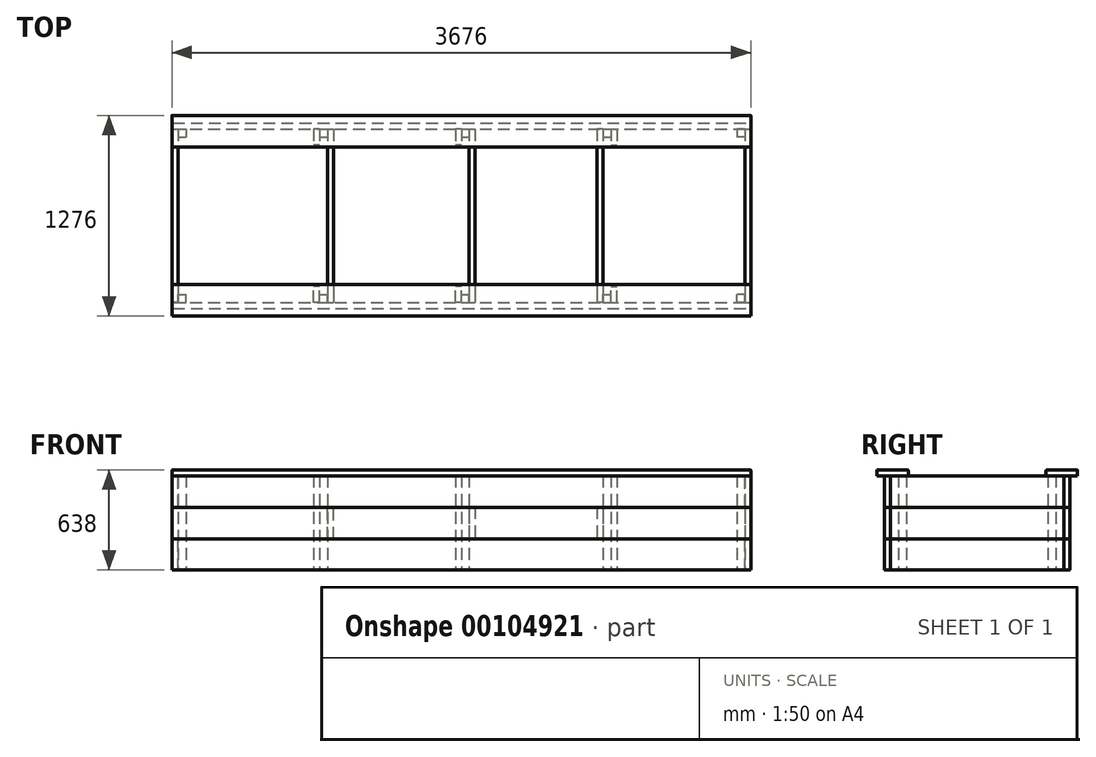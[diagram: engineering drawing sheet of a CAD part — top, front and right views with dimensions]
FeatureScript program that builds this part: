
annotation { "Feature Type Name" : "Feature", "Feature Type Description" : "" }
export const myFeature = defineFeature(function(context is Context, id is Id, definition is map)
    precondition{}
    {
        {
            var Q0;
            Q0=qCreatedBy(makeId("Top.planeOp"),FACE);
            var sketch = newSketch(context, id + "F0", { "sketchPlane" : qUnion([Q0])});
            skLineSegment(sketch, "E0", {"start": v(-110.58, 50) * mm, "end": v(3489.42, 50) * mm, "construction": true});
            skLineSegment(sketch, "E1", {"start": v(3489.42, 50) * mm, "end": v(3489.42, -1050) * mm, "construction": true});
            skLineSegment(sketch, "E2", {"start": v(3489.42, -1050) * mm, "end": v(-110.58, -1050) * mm, "construction": true});
            skLineSegment(sketch, "E3", {"start": v(-110.58, -1050) * mm, "end": v(-110.58, 50) * mm, "construction": true});
            skLineSegment(sketch, "E4.bottom", {"start": v(-110.58, 50) * mm, "end": v(-60.58, 50) * mm});
            skLineSegment(sketch, "E4.top", {"start": v(-110.58, 0) * mm, "end": v(-60.58, 0) * mm});
            skLineSegment(sketch, "E4.left", {"start": v(-110.58, 50) * mm, "end": v(-110.58, 0) * mm});
            skLineSegment(sketch, "E4.right", {"start": v(-60.58, 50) * mm, "end": v(-60.58, 0) * mm});
            skLineSegment(sketch, "E5.bottom", {"start": v(-110.58, -1050) * mm, "end": v(-60.58, -1050) * mm});
            skLineSegment(sketch, "E5.top", {"start": v(-110.58, -1000) * mm, "end": v(-60.58, -1000) * mm});
            skLineSegment(sketch, "E5.left", {"start": v(-110.58, -1050) * mm, "end": v(-110.58, -1000) * mm});
            skLineSegment(sketch, "E5.right", {"start": v(-60.58, -1050) * mm, "end": v(-60.58, -1000) * mm});
            skLineSegment(sketch, "E6.bottom", {"start": v(3489.42, -1050) * mm, "end": v(3439.42, -1050) * mm});
            skLineSegment(sketch, "E6.top", {"start": v(3489.42, -1000) * mm, "end": v(3439.42, -1000) * mm});
            skLineSegment(sketch, "E6.left", {"start": v(3489.42, -1050) * mm, "end": v(3489.42, -1000) * mm});
            skLineSegment(sketch, "E6.right", {"start": v(3439.42, -1050) * mm, "end": v(3439.42, -1000) * mm});
            skLineSegment(sketch, "E7.bottom", {"start": v(3489.42, 50) * mm, "end": v(3439.42, 50) * mm});
            skLineSegment(sketch, "E7.top", {"start": v(3489.42, 0) * mm, "end": v(3439.42, 0) * mm});
            skLineSegment(sketch, "E7.left", {"start": v(3489.42, 50) * mm, "end": v(3489.42, 0) * mm});
            skLineSegment(sketch, "E7.right", {"start": v(3439.42, 50) * mm, "end": v(3439.42, 0) * mm});
            skLineSegment(sketch, "E8.bottom", {"start": v(789.42, -1050) * mm, "end": v(839.42, -1050) * mm});
            skLineSegment(sketch, "E8.top", {"start": v(789.42, -1000) * mm, "end": v(839.42, -1000) * mm});
            skLineSegment(sketch, "E8.left", {"start": v(789.42, -1050) * mm, "end": v(789.42, -1000) * mm});
            skLineSegment(sketch, "E8.right", {"start": v(839.42, -1050) * mm, "end": v(839.42, -1000) * mm});
            skLineSegment(sketch, "E9.bottom", {"start": v(1689.42, -1050) * mm, "end": v(1739.42, -1050) * mm});
            skLineSegment(sketch, "E9.top", {"start": v(1689.42, -1000) * mm, "end": v(1739.42, -1000) * mm});
            skLineSegment(sketch, "E9.left", {"start": v(1689.42, -1050) * mm, "end": v(1689.42, -1000) * mm});
            skLineSegment(sketch, "E9.right", {"start": v(1739.42, -1050) * mm, "end": v(1739.42, -1000) * mm});
            skLineSegment(sketch, "E10.bottom", {"start": v(2589.42, -1050) * mm, "end": v(2639.42, -1050) * mm});
            skLineSegment(sketch, "E10.top", {"start": v(2589.42, -1000) * mm, "end": v(2639.42, -1000) * mm});
            skLineSegment(sketch, "E10.left", {"start": v(2589.42, -1050) * mm, "end": v(2589.42, -1000) * mm});
            skLineSegment(sketch, "E10.right", {"start": v(2639.42, -1050) * mm, "end": v(2639.42, -1000) * mm});
            skLineSegment(sketch, "E11.bottom", {"start": v(789.42, 50) * mm, "end": v(839.42, 50) * mm});
            skLineSegment(sketch, "E11.top", {"start": v(789.42, 0) * mm, "end": v(839.42, 0) * mm});
            skLineSegment(sketch, "E11.left", {"start": v(789.42, 50) * mm, "end": v(789.42, 0) * mm});
            skLineSegment(sketch, "E11.right", {"start": v(839.42, 50) * mm, "end": v(839.42, 0) * mm});
            skLineSegment(sketch, "E12.bottom", {"start": v(1689.42, 50) * mm, "end": v(1739.42, 50) * mm});
            skLineSegment(sketch, "E12.top", {"start": v(1689.42, 0) * mm, "end": v(1739.42, 0) * mm});
            skLineSegment(sketch, "E12.left", {"start": v(1689.42, 50) * mm, "end": v(1689.42, 0) * mm});
            skLineSegment(sketch, "E12.right", {"start": v(1739.42, 50) * mm, "end": v(1739.42, 0) * mm});
            skLineSegment(sketch, "E13.bottom", {"start": v(2589.42, 50) * mm, "end": v(2639.42, 50) * mm});
            skLineSegment(sketch, "E13.top", {"start": v(2589.42, 0) * mm, "end": v(2639.42, 0) * mm});
            skLineSegment(sketch, "E13.left", {"start": v(2589.42, 50) * mm, "end": v(2589.42, 0) * mm});
            skLineSegment(sketch, "E13.right", {"start": v(2639.42, 50) * mm, "end": v(2639.42, 0) * mm});
            skLineSegment(sketch, "E14.bottom", {"start": v(789.42, 50) * mm, "end": v(751.42, 50) * mm});
            skLineSegment(sketch, "E14.top", {"start": v(789.42, -50) * mm, "end": v(751.42, -50) * mm});
            skLineSegment(sketch, "E14.left", {"start": v(789.42, 50) * mm, "end": v(789.42, -50) * mm});
            skLineSegment(sketch, "E14.right", {"start": v(751.42, 50) * mm, "end": v(751.42, -50) * mm});
            skLineSegment(sketch, "E15.bottom", {"start": v(1689.42, 50) * mm, "end": v(1651.42, 50) * mm});
            skLineSegment(sketch, "E15.top", {"start": v(1689.42, -50) * mm, "end": v(1651.42, -50) * mm});
            skLineSegment(sketch, "E15.left", {"start": v(1689.42, 50) * mm, "end": v(1689.42, -50) * mm});
            skLineSegment(sketch, "E15.right", {"start": v(1651.42, 50) * mm, "end": v(1651.42, -50) * mm});
            skLineSegment(sketch, "E16.bottom", {"start": v(789.42, -1050) * mm, "end": v(751.42, -1050) * mm});
            skLineSegment(sketch, "E16.top", {"start": v(789.42, -950) * mm, "end": v(751.42, -950) * mm});
            skLineSegment(sketch, "E16.left", {"start": v(789.42, -1050) * mm, "end": v(789.42, -950) * mm});
            skLineSegment(sketch, "E16.right", {"start": v(751.42, -1050) * mm, "end": v(751.42, -950) * mm});
            skLineSegment(sketch, "E17.bottom", {"start": v(1689.42, -1050) * mm, "end": v(1651.42, -1050) * mm});
            skLineSegment(sketch, "E17.top", {"start": v(1689.42, -950) * mm, "end": v(1651.42, -950) * mm});
            skLineSegment(sketch, "E17.left", {"start": v(1689.42, -1050) * mm, "end": v(1689.42, -950) * mm});
            skLineSegment(sketch, "E17.right", {"start": v(1651.42, -1050) * mm, "end": v(1651.42, -950) * mm});
            skLineSegment(sketch, "E18.bottom", {"start": v(2639.42, 50) * mm, "end": v(2677.42, 50) * mm});
            skLineSegment(sketch, "E18.top", {"start": v(2639.42, -50) * mm, "end": v(2677.42, -50) * mm});
            skLineSegment(sketch, "E18.left", {"start": v(2639.42, 50) * mm, "end": v(2639.42, -50) * mm});
            skLineSegment(sketch, "E18.right", {"start": v(2677.42, 50) * mm, "end": v(2677.42, -50) * mm});
            skLineSegment(sketch, "E19.bottom", {"start": v(2639.42, -1050) * mm, "end": v(2677.42, -1050) * mm});
            skLineSegment(sketch, "E19.top", {"start": v(2639.42, -950) * mm, "end": v(2677.42, -950) * mm});
            skLineSegment(sketch, "E19.left", {"start": v(2639.42, -1050) * mm, "end": v(2639.42, -950) * mm});
            skLineSegment(sketch, "E19.right", {"start": v(2677.42, -1050) * mm, "end": v(2677.42, -950) * mm});
            skSolve(sketch);
        }
        {
            var Q0;
            Q0=makeQuery(id+"F0.imprint","IMPRINT",FACE,{"disambiguationData":[TD([[makeQuery(id+"F0.imprint","IMPRINT",EDGE,{"derivedFrom":sQuery(id+"F0.wireOp",EDGE,"E4.bottom")}),-1.0]])]});
            var Q1;
            {var subQ0=sQuery(id+"F0.wireOp",EDGE,"E11.bottom");Q1=makeQuery(id+"F0.imprint","IMPRINT",FACE,{"disambiguationData":[TD([[makeQuery(id+"F0.imprint","IMPRINT",EDGE,{"derivedFrom":subQ0}),-1.0]])]});}
            var Q2;
            {var subQ0=sQuery(id+"F0.wireOp",EDGE,"E12.bottom");Q2=makeQuery(id+"F0.imprint","IMPRINT",FACE,{"disambiguationData":[TD([[makeQuery(id+"F0.imprint","IMPRINT",EDGE,{"derivedFrom":subQ0}),-1.0]])]});}
            var Q3;
            {var subQ0=sQuery(id+"F0.wireOp",EDGE,"E13.bottom");Q3=makeQuery(id+"F0.imprint","IMPRINT",FACE,{"disambiguationData":[TD([[makeQuery(id+"F0.imprint","IMPRINT",EDGE,{"derivedFrom":subQ0}),-1.0]])]});}
            var Q4;
            Q4=makeQuery(id+"F0.imprint","IMPRINT",FACE,{"disambiguationData":[TD([[makeQuery(id+"F0.imprint","IMPRINT",EDGE,{"derivedFrom":sQuery(id+"F0.wireOp",EDGE,"E7.bottom")}),1.0]])]});
            var Q5;
            Q5=makeQuery(id+"F0.imprint","IMPRINT",FACE,{"disambiguationData":[TD([[makeQuery(id+"F0.imprint","IMPRINT",EDGE,{"derivedFrom":sQuery(id+"F0.wireOp",EDGE,"E6.bottom")}),-1.0]])]});
            var Q6;
            {var subQ0=sQuery(id+"F0.wireOp",EDGE,"E10.bottom");Q6=makeQuery(id+"F0.imprint","IMPRINT",FACE,{"disambiguationData":[TD([[makeQuery(id+"F0.imprint","IMPRINT",EDGE,{"derivedFrom":subQ0}),1.0]])]});}
            var Q7;
            {var subQ0=sQuery(id+"F0.wireOp",EDGE,"E9.bottom");Q7=makeQuery(id+"F0.imprint","IMPRINT",FACE,{"disambiguationData":[TD([[makeQuery(id+"F0.imprint","IMPRINT",EDGE,{"derivedFrom":subQ0}),1.0]])]});}
            var Q8;
            {var subQ0=sQuery(id+"F0.wireOp",EDGE,"E8.bottom");Q8=makeQuery(id+"F0.imprint","IMPRINT",FACE,{"disambiguationData":[TD([[makeQuery(id+"F0.imprint","IMPRINT",EDGE,{"derivedFrom":subQ0}),1.0]])]});}
            var Q9;
            Q9=makeQuery(id+"F0.imprint","IMPRINT",FACE,{"disambiguationData":[TD([[makeQuery(id+"F0.imprint","IMPRINT",EDGE,{"derivedFrom":sQuery(id+"F0.wireOp",EDGE,"E5.bottom")}),1.0]])]});
            extrude(context, id + "F1", {"entities" : qUnion([Q0, Q1, Q2, Q3, Q4, Q5, Q6, Q7, Q8, Q9]), "depth" : 600 * mm});
        }
        {
            var Q0;
            {var subQ3=sQuery(id+"F0.wireOp",EDGE,"E14.bottom");Q0=makeQuery(id+"F0.imprint","IMPRINT",FACE,{"disambiguationData":[TD([[makeQuery(id+"F0.imprint","IMPRINT",EDGE,{"derivedFrom":subQ3}),1.0]])]});}
            var Q1;
            {var subQ3=sQuery(id+"F0.wireOp",EDGE,"E16.bottom");Q1=makeQuery(id+"F0.imprint","IMPRINT",FACE,{"disambiguationData":[TD([[makeQuery(id+"F0.imprint","IMPRINT",EDGE,{"derivedFrom":subQ3}),-1.0]])]});}
            var Q2;
            {var subQ3=sQuery(id+"F0.wireOp",EDGE,"E15.bottom");Q2=makeQuery(id+"F0.imprint","IMPRINT",FACE,{"disambiguationData":[TD([[makeQuery(id+"F0.imprint","IMPRINT",EDGE,{"derivedFrom":subQ3}),1.0]])]});}
            var Q3;
            {var subQ3=sQuery(id+"F0.wireOp",EDGE,"E17.bottom");Q3=makeQuery(id+"F0.imprint","IMPRINT",FACE,{"disambiguationData":[TD([[makeQuery(id+"F0.imprint","IMPRINT",EDGE,{"derivedFrom":subQ3}),-1.0]])]});}
            var Q4;
            {var subQ3=sQuery(id+"F0.wireOp",EDGE,"E18.bottom");Q4=makeQuery(id+"F0.imprint","IMPRINT",FACE,{"disambiguationData":[TD([[makeQuery(id+"F0.imprint","IMPRINT",EDGE,{"derivedFrom":subQ3}),-1.0]])]});}
            var Q5;
            {var subQ3=sQuery(id+"F0.wireOp",EDGE,"E19.bottom");Q5=makeQuery(id+"F0.imprint","IMPRINT",FACE,{"disambiguationData":[TD([[makeQuery(id+"F0.imprint","IMPRINT",EDGE,{"derivedFrom":subQ3}),1.0]])]});}
            extrude(context, id + "F2", {"entities" : qUnion([Q0, Q1, Q2, Q3, Q4, Q5]), "depth" : 600 * mm});
        }
        {
            var Q0;
            Q0=makeQuery(id+"F1.opExtrude","SWEPT_FACE",FACE,{"disambiguationData":[OSD([sQuery(id+"F0.wireOp",EDGE,"E5.bottom")])]});
            var sketch = newSketch(context, id + "F3", { "sketchPlane" : qUnion([Q0])});
            skLineSegment(sketch, "E20.0", {"start": v(-110.58, 0) * mm, "end": v(-60.58, 0) * mm, "construction": true});
            skLineSegment(sketch, "E21.0", {"start": v(-110.58, 200) * mm, "end": v(-60.58, 200) * mm, "construction": true});
            skLineSegment(sketch, "E22.0", {"start": v(839.42, 600) * mm, "end": v(839.42, 0) * mm, "construction": true});
            skLineSegment(sketch, "E22.1", {"start": v(1739.42, 600) * mm, "end": v(1739.42, 0) * mm, "construction": true});
            skLineSegment(sketch, "E22.2", {"start": v(2589.42, 600) * mm, "end": v(2589.42, 0) * mm, "construction": true});
            skLineSegment(sketch, "E23.bottom", {"start": v(839.42, 200) * mm, "end": v(877.42, 200) * mm});
            skLineSegment(sketch, "E23.top", {"start": v(839.42, 400) * mm, "end": v(877.42, 400) * mm});
            skLineSegment(sketch, "E23.left", {"start": v(839.42, 200) * mm, "end": v(839.42, 400) * mm});
            skLineSegment(sketch, "E23.right", {"start": v(877.42, 200) * mm, "end": v(877.42, 400) * mm});
            skLineSegment(sketch, "E24.bottom", {"start": v(1739.42, 400) * mm, "end": v(1777.42, 400) * mm});
            skLineSegment(sketch, "E24.top", {"start": v(1739.42, 200) * mm, "end": v(1777.42, 200) * mm});
            skLineSegment(sketch, "E24.left", {"start": v(1739.42, 400) * mm, "end": v(1739.42, 200) * mm});
            skLineSegment(sketch, "E24.right", {"start": v(1777.42, 400) * mm, "end": v(1777.42, 200) * mm});
            skLineSegment(sketch, "E25.bottom", {"start": v(2589.42, 400) * mm, "end": v(2551.42, 400) * mm});
            skLineSegment(sketch, "E25.top", {"start": v(2589.42, 200) * mm, "end": v(2551.42, 200) * mm});
            skLineSegment(sketch, "E25.left", {"start": v(2589.42, 400) * mm, "end": v(2589.42, 200) * mm});
            skLineSegment(sketch, "E25.right", {"start": v(2551.42, 400) * mm, "end": v(2551.42, 200) * mm});
            skLineSegment(sketch, "E26.0", {"start": v(-110.58, 600) * mm, "end": v(-110.58, 0) * mm});
            skLineSegment(sketch, "E26.1", {"start": v(3489.42, 600) * mm, "end": v(3489.42, 0) * mm});
            skLineSegment(sketch, "E27.bottom", {"start": v(-110.58, 0) * mm, "end": v(-148.58, 0) * mm});
            skLineSegment(sketch, "E27.top", {"start": v(-110.58, 200) * mm, "end": v(-148.58, 200) * mm});
            skLineSegment(sketch, "E27.left", {"start": v(-110.58, 0) * mm, "end": v(-110.58, 200) * mm});
            skLineSegment(sketch, "E27.right", {"start": v(-148.58, 0) * mm, "end": v(-148.58, 200) * mm});
            skLineSegment(sketch, "E28.top", {"start": v(-110.58, 400) * mm, "end": v(-148.58, 400) * mm});
            skLineSegment(sketch, "E28.left", {"start": v(-110.58, 200) * mm, "end": v(-110.58, 400) * mm});
            skLineSegment(sketch, "E28.right", {"start": v(-148.58, 200) * mm, "end": v(-148.58, 400) * mm});
            skLineSegment(sketch, "E29.top", {"start": v(-110.58, 600) * mm, "end": v(-148.58, 600) * mm});
            skLineSegment(sketch, "E29.left", {"start": v(-110.58, 400) * mm, "end": v(-110.58, 600) * mm});
            skLineSegment(sketch, "E29.right", {"start": v(-148.58, 400) * mm, "end": v(-148.58, 600) * mm});
            skPoint(sketch, "E30.oppositeSnap0", {"position": v(-85.58, 200) * mm});
            skLineSegment(sketch, "E30.bottom", {"start": v(3489.42, 0) * mm, "end": v(3527.42, 0) * mm});
            skLineSegment(sketch, "E30.top", {"start": v(3489.42, 200) * mm, "end": v(3527.42, 200) * mm});
            skLineSegment(sketch, "E30.left", {"start": v(3489.42, 0) * mm, "end": v(3489.42, 200) * mm});
            skLineSegment(sketch, "E30.right", {"start": v(3527.42, 0) * mm, "end": v(3527.42, 200) * mm});
            skLineSegment(sketch, "E31.top", {"start": v(3489.42, 400) * mm, "end": v(3527.42, 400) * mm});
            skLineSegment(sketch, "E31.left", {"start": v(3489.42, 200) * mm, "end": v(3489.42, 400) * mm});
            skLineSegment(sketch, "E31.right", {"start": v(3527.42, 200) * mm, "end": v(3527.42, 400) * mm});
            skLineSegment(sketch, "E32.top", {"start": v(3489.42, 600) * mm, "end": v(3527.42, 600) * mm});
            skLineSegment(sketch, "E32.left", {"start": v(3489.42, 400) * mm, "end": v(3489.42, 600) * mm});
            skLineSegment(sketch, "E32.right", {"start": v(3527.42, 400) * mm, "end": v(3527.42, 600) * mm});
            skSolve(sketch);
        }
        {
            var Q0;
            Q0=makeQuery(id+"F3.imprint","IMPRINT",FACE,{"disambiguationData":[TD([[makeQuery(id+"F3.imprint","IMPRINT",EDGE,{"derivedFrom":sQuery(id+"F3.wireOp",EDGE,"E30.top")}),1.0]])]});
            var Q1;
            Q1=makeQuery(id+"F3.imprint","IMPRINT",FACE,{"disambiguationData":[TD([[makeQuery(id+"F3.imprint","IMPRINT",EDGE,{"derivedFrom":sQuery(id+"F3.wireOp",EDGE,"E25.bottom")}),1.0]])]});
            var Q2;
            Q2=makeQuery(id+"F3.imprint","IMPRINT",FACE,{"disambiguationData":[TD([[makeQuery(id+"F3.imprint","IMPRINT",EDGE,{"derivedFrom":sQuery(id+"F3.wireOp",EDGE,"E24.bottom")}),-1.0]])]});
            var Q3;
            Q3=makeQuery(id+"F3.imprint","IMPRINT",FACE,{"disambiguationData":[TD([[makeQuery(id+"F3.imprint","IMPRINT",EDGE,{"derivedFrom":sQuery(id+"F3.wireOp",EDGE,"E23.bottom")}),1.0]])]});
            var Q4;
            Q4=makeQuery(id+"F3.imprint","IMPRINT",FACE,{"disambiguationData":[TD([[makeQuery(id+"F3.imprint","IMPRINT",EDGE,{"derivedFrom":sQuery(id+"F3.wireOp",EDGE,"E27.top")}),-1.0]])]});
            var Q5;
            Q5=makeQuery(id+"F1.opExtrude","SWEPT_FACE",FACE,{"disambiguationData":[OSD([sQuery(id+"F0.wireOp",EDGE,"E4.bottom")])]});
            extrude(context, id + "F4", {"entities" : qUnion([Q0, Q1, Q2, Q3, Q4]), "endBound" : BoundingType.UP_TO_SURFACE, "oppositeDirection" : true, "endBoundEntityFace" : qUnion([Q5]), "depth" : 25 * mm});
        }
        {
            var Q0;
            Q0=makeQuery(id+"F3.imprint","IMPRINT",FACE,{"disambiguationData":[TD([[makeQuery(id+"F3.imprint","IMPRINT",EDGE,{"derivedFrom":sQuery(id+"F3.wireOp",EDGE,"E31.top")}),1.0]])]});
            var Q1;
            Q1=makeQuery(id+"F3.imprint","IMPRINT",FACE,{"disambiguationData":[TD([[makeQuery(id+"F3.imprint","IMPRINT",EDGE,{"derivedFrom":sQuery(id+"F3.wireOp",EDGE,"E30.bottom")}),1.0]])]});
            var Q2;
            Q2=makeQuery(id+"F3.imprint","IMPRINT",FACE,{"disambiguationData":[TD([[makeQuery(id+"F3.imprint","IMPRINT",EDGE,{"derivedFrom":sQuery(id+"F3.wireOp",EDGE,"E28.top")}),-1.0]])]});
            var Q3;
            Q3=makeQuery(id+"F3.imprint","IMPRINT",FACE,{"disambiguationData":[TD([[makeQuery(id+"F3.imprint","IMPRINT",EDGE,{"derivedFrom":sQuery(id+"F3.wireOp",EDGE,"E27.bottom")}),-1.0]])]});
            var Q4;
            Q4=makeQuery(id+"F1.opExtrude","SWEPT_FACE",FACE,{"disambiguationData":[OSD([sQuery(id+"F0.wireOp",EDGE,"E7.bottom")])]});
            extrude(context, id + "F5", {"entities" : qUnion([Q0, Q1, Q2, Q3]), "endBound" : BoundingType.UP_TO_SURFACE, "oppositeDirection" : true, "endBoundEntityFace" : qUnion([Q4]), "depth" : 25 * mm});
        }
        {
            var Q0;
            Q0=makeQuery(id+"F1.opExtrude","SWEPT_FACE",FACE,{"disambiguationData":[OSD([sQuery(id+"F0.wireOp",EDGE,"E7.left")])]});
            var sketch = newSketch(context, id + "F6", { "sketchPlane" : qUnion([Q0])});
            skLineSegment(sketch, "E33.bottom", {"start": v(50, 600) * mm, "end": v(88, 600) * mm});
            skLineSegment(sketch, "E33.top", {"start": v(50, 400) * mm, "end": v(88, 400) * mm});
            skLineSegment(sketch, "E33.left", {"start": v(50, 600) * mm, "end": v(50, 400) * mm});
            skLineSegment(sketch, "E33.right", {"start": v(88, 600) * mm, "end": v(88, 400) * mm});
            skLineSegment(sketch, "E34.top", {"start": v(50, 200) * mm, "end": v(88, 200) * mm});
            skLineSegment(sketch, "E34.left", {"start": v(50, 400) * mm, "end": v(50, 200) * mm});
            skLineSegment(sketch, "E34.right", {"start": v(88, 400) * mm, "end": v(88, 200) * mm});
            skLineSegment(sketch, "E35.top", {"start": v(50, 0) * mm, "end": v(88, 0) * mm});
            skLineSegment(sketch, "E35.left", {"start": v(50, 200) * mm, "end": v(50, 0) * mm});
            skLineSegment(sketch, "E35.right", {"start": v(88, 200) * mm, "end": v(88, 0) * mm});
            skLineSegment(sketch, "E36.0", {"start": v(-1050, 400) * mm, "end": v(-1050, 600) * mm, "construction": true});
            skLineSegment(sketch, "E37.bottom", {"start": v(-1050, 600) * mm, "end": v(-1088, 600) * mm});
            skLineSegment(sketch, "E37.top", {"start": v(-1050, 400) * mm, "end": v(-1088, 400) * mm});
            skLineSegment(sketch, "E37.left", {"start": v(-1050, 600) * mm, "end": v(-1050, 400) * mm});
            skLineSegment(sketch, "E37.right", {"start": v(-1088, 600) * mm, "end": v(-1088, 400) * mm});
            skLineSegment(sketch, "E38.top", {"start": v(-1050, 200) * mm, "end": v(-1088, 200) * mm});
            skLineSegment(sketch, "E38.left", {"start": v(-1050, 400) * mm, "end": v(-1050, 200) * mm});
            skLineSegment(sketch, "E38.right", {"start": v(-1088, 400) * mm, "end": v(-1088, 200) * mm});
            skLineSegment(sketch, "E39.top", {"start": v(-1050, 0) * mm, "end": v(-1088, 0) * mm});
            skLineSegment(sketch, "E39.left", {"start": v(-1050, 200) * mm, "end": v(-1050, 0) * mm});
            skLineSegment(sketch, "E39.right", {"start": v(-1088, 200) * mm, "end": v(-1088, 0) * mm});
            skLineSegment(sketch, "E40.bottom", {"start": v(-938, 600) * mm, "end": v(-1138, 600) * mm});
            skLineSegment(sketch, "E40.top", {"start": v(-938, 638) * mm, "end": v(-1138, 638) * mm});
            skLineSegment(sketch, "E40.left", {"start": v(-938, 600) * mm, "end": v(-938, 638) * mm});
            skLineSegment(sketch, "E40.right", {"start": v(-1138, 600) * mm, "end": v(-1138, 638) * mm});
            skLineSegment(sketch, "E41.bottom", {"start": v(-1088, 600) * mm, "end": v(-1138, 600) * mm});
            skLineSegment(sketch, "E41.top", {"start": v(-1088, 600) * mm, "end": v(-1138, 600) * mm});
            skLineSegment(sketch, "E41.left", {"start": v(-1088, 600) * mm, "end": v(-1088, 600) * mm});
            skLineSegment(sketch, "E41.right", {"start": v(-1138, 600) * mm, "end": v(-1138, 600) * mm});
            skLineSegment(sketch, "E42.bottom", {"start": v(-62, 638) * mm, "end": v(138, 638) * mm});
            skLineSegment(sketch, "E42.top", {"start": v(-62, 600) * mm, "end": v(138, 600) * mm});
            skLineSegment(sketch, "E42.left", {"start": v(-62, 638) * mm, "end": v(-62, 600) * mm});
            skLineSegment(sketch, "E42.right", {"start": v(138, 638) * mm, "end": v(138, 600) * mm});
            skSolve(sketch);
        }
        {
            var Q0;
            {var subQ0=sQuery(id+"F6.wireOp",EDGE,"E37.left");Q0=makeQuery(id+"F6.imprint","IMPRINT",FACE,{"disambiguationData":[TD([[makeQuery(id+"F6.imprint","IMPRINT",EDGE,{"derivedFrom":subQ0}),-1.0]])]});}
            var Q1;
            Q1=makeQuery(id+"F6.imprint","IMPRINT",FACE,{"disambiguationData":[TD([[makeQuery(id+"F6.imprint","IMPRINT",EDGE,{"derivedFrom":sQuery(id+"F6.wireOp",EDGE,"E38.top")}),1.0]])]});
            var Q2;
            {var subQ0=sQuery(id+"F6.wireOp",EDGE,"E33.left");Q2=makeQuery(id+"F6.imprint","IMPRINT",FACE,{"disambiguationData":[TD([[makeQuery(id+"F6.imprint","IMPRINT",EDGE,{"derivedFrom":subQ0}),1.0]])]});}
            var Q3;
            Q3=makeQuery(id+"F6.imprint","IMPRINT",FACE,{"disambiguationData":[TD([[makeQuery(id+"F6.imprint","IMPRINT",EDGE,{"derivedFrom":sQuery(id+"F6.wireOp",EDGE,"E34.top")}),-1.0]])]});
            var Q4;
            Q4=makeQuery(id+"F5.opExtrude","SWEPT_FACE",FACE,{"disambiguationData":[OSD([sQuery(id+"F3.wireOp",EDGE,"E29.right")])]});
            var Q5;
            Q5=makeQuery(id+"F4.opExtrude","SWEPT_FACE",FACE,{"disambiguationData":[OSD([sQuery(id+"F3.wireOp",EDGE,"E31.right")])]});
            extrude(context, id + "F7", {"entities" : qUnion([Q0, Q1, Q2, Q3]), "endBound" : BoundingType.UP_TO_SURFACE, "oppositeDirection" : true, "endBoundEntityFace" : qUnion([Q4]), "depth" : 25 * mm, "hasSecondDirection" : true, "secondDirectionBound" : SecondDirectionBoundingType.UP_TO_SURFACE, "secondDirectionOppositeDirection" : false, "secondDirectionBoundEntityFace" : qUnion([Q5]), "secondDirectionDepth" : 25 * mm});
        }
        {
            var Q0;
            Q0=makeQuery(id+"F6.imprint","IMPRINT",FACE,{"disambiguationData":[TD([[makeQuery(id+"F6.imprint","IMPRINT",EDGE,{"derivedFrom":sQuery(id+"F6.wireOp",EDGE,"E37.top")}),1.0]])]});
            var Q1;
            Q1=makeQuery(id+"F6.imprint","IMPRINT",FACE,{"disambiguationData":[TD([[makeQuery(id+"F6.imprint","IMPRINT",EDGE,{"derivedFrom":sQuery(id+"F6.wireOp",EDGE,"E33.top")}),-1.0]])]});
            var Q2;
            Q2=makeQuery(id+"F6.imprint","IMPRINT",FACE,{"disambiguationData":[TD([[makeQuery(id+"F6.imprint","IMPRINT",EDGE,{"derivedFrom":sQuery(id+"F6.wireOp",EDGE,"E40.top")}),1.0]])]});
            var Q3;
            Q3=makeQuery(id+"F6.imprint","IMPRINT",FACE,{"disambiguationData":[TD([[makeQuery(id+"F6.imprint","IMPRINT",EDGE,{"derivedFrom":sQuery(id+"F6.wireOp",EDGE,"E42.bottom")}),-1.0]])]});
            var Q4;
            Q4=makeQuery(id+"F5.opExtrude","SWEPT_FACE",FACE,{"disambiguationData":[OSD([sQuery(id+"F3.wireOp",EDGE,"E29.right")])]});
            var Q5;
            Q5=makeQuery(id+"F4.opExtrude","SWEPT_FACE",FACE,{"disambiguationData":[OSD([sQuery(id+"F3.wireOp",EDGE,"E31.right")])]});
            extrude(context, id + "F8", {"entities" : qUnion([Q0, Q1, Q2, Q3]), "endBound" : BoundingType.UP_TO_SURFACE, "oppositeDirection" : true, "endBoundEntityFace" : qUnion([Q4]), "depth" : 25 * mm, "hasSecondDirection" : true, "secondDirectionBound" : SecondDirectionBoundingType.UP_TO_SURFACE, "secondDirectionOppositeDirection" : false, "secondDirectionBoundEntityFace" : qUnion([Q5]), "secondDirectionDepth" : 25 * mm});
        }
        {
            var Q0;
            Q0=makeQuery(id+"F7.opExtrude","SWEPT_FACE",FACE,{"disambiguationData":[OSD([sQuery(id+"F6.wireOp",EDGE,"E37.right")])]});
            var Q1;
            Q1=makeQuery(id+"F8.opExtrude","SWEPT_FACE",FACE,{"disambiguationData":[OSD([sQuery(id+"F6.wireOp",EDGE,"E38.right")])]});
            var Q2;
            Q2=makeQuery(id+"F7.opExtrude","SWEPT_FACE",FACE,{"disambiguationData":[OSD([sQuery(id+"F6.wireOp",EDGE,"E39.right")])]});
            var Q3;
            Q3=makeQuery(id+"F5.opExtrude","SWEPT_FACE",FACE,{"disambiguationData":[OSD([sQuery(id+"F3.wireOp",EDGE,"E27.right")])]});
            var Q4;
            Q4=makeQuery(id+"F4.opExtrude","SWEPT_FACE",FACE,{"disambiguationData":[OSD([sQuery(id+"F3.wireOp",EDGE,"E28.right")])]});
            var Q5;
            Q5=makeQuery(id+"F5.opExtrude","SWEPT_FACE",FACE,{"disambiguationData":[OSD([sQuery(id+"F3.wireOp",EDGE,"E29.right")])]});
            var Q6;
            Q6=makeQuery(id+"F7.opExtrude","SWEPT_FACE",FACE,{"disambiguationData":[OSD([sQuery(id+"F6.wireOp",EDGE,"E33.right")])]});
            var Q7;
            Q7=makeQuery(id+"F8.opExtrude","SWEPT_FACE",FACE,{"disambiguationData":[OSD([sQuery(id+"F6.wireOp",EDGE,"E34.right")])]});
            var Q8;
            Q8=makeQuery(id+"F7.opExtrude","SWEPT_FACE",FACE,{"disambiguationData":[OSD([sQuery(id+"F6.wireOp",EDGE,"E35.right")])]});
            var Q9;
            Q9=makeQuery(id+"F5.opExtrude","SWEPT_FACE",FACE,{"disambiguationData":[OSD([sQuery(id+"F3.wireOp",EDGE,"E32.right")])]});
            var Q10;
            Q10=makeQuery(id+"F4.opExtrude","SWEPT_FACE",FACE,{"disambiguationData":[OSD([sQuery(id+"F3.wireOp",EDGE,"E31.right")])]});
            var Q11;
            Q11=makeQuery(id+"F5.opExtrude","SWEPT_FACE",FACE,{"disambiguationData":[OSD([sQuery(id+"F3.wireOp",EDGE,"E30.right")])]});
            var Q12;
            Q12=makeQuery(id+"F8.opExtrude","SWEPT_FACE",FACE,{"disambiguationData":[OSD([sQuery(id+"F6.wireOp",EDGE,"E40.top")])]});
            var Q13;
            Q13=makeQuery(id+"F8.opExtrude","SWEPT_FACE",FACE,{"disambiguationData":[OSD([sQuery(id+"F6.wireOp",EDGE,"E42.bottom")])]});
            fillet(context, id + "F9", {"entities" : qUnion([Q0, Q1, Q2, Q3, Q4, Q5, Q6, Q7, Q8, Q9, Q10, Q11, Q12, Q13]), "radius" : 5 * mm, "tangentPropagation" : true, "allowEdgeOverflow" : false});
        }
    });
